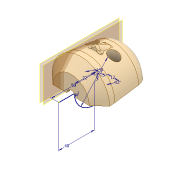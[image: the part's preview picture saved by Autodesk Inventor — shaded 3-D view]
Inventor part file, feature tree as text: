
AUTODESK INVENTOR PART (.ipt)
format: ipt  version: 2017 (Build 210142000, 142)  size: 439,808 bytes
history: native  units: mm
features: sketch x14, extrude x11, fillet x7, chamfer x2, plane x2, projected_geometry x2, revolve x1, thicken_offset x1
ambient origin geometry x8: Origin, YZ Plane, XZ Plane, XY Plane, X Axis, Y Axis, Z Axis, Center Point
bodies: Solid1 (feature_tree)
feature tree (40):
  revolve  "Revolution1"  [1 undecoded]
  fillet  "Fillet1"  Radius=30.0mm
  chamfer  "Chamfer1"  Distance=10.0mm Angle=45.0deg
  fillet  "Fillet2"  Radius=20.0mm
  fillet  "Fillet3"  Radius=60.0mm
  thicken_offset  "Thicken1"
  extrude  "Extrusion1"  Depth=4.0mm
  sketch  "Sketch3"  dims[d4=20.0mm d5=10.0mm d6=20.0mm d7=45.0deg d8=20.0mm d9=60.0mm]
  extrude  "Extrusion2"  Depth=50.0mm
  extrude  "Extrusion3"  Depth=12.0mm
  fillet  "Fillet4"  Radius=12.0mm
  fillet  "Fillet5"  Radius=12.0mm
  extrude  "Extrusion4"  Depth=10.0mm TaperAngle=0.0deg
  fillet  "Fillet6"  Radius=6.0mm
  fillet  "Fillet7"  Radius=2.0mm
  extrude  "Extrusion5"  Depth=5.0mm
  sketch  "Sketch7"  dims[d20=10.0mm d21=0.0mm d22=10.0mm d23=0.0mm d24=6.0mm d25=2.0mm]
  plane  "Work Plane1"
  extrude  "Extrusion6"  Depth=2.0mm
  extrude  "Extrusion7"  Depth=40.0mm
  extrude  "Extrusion8"  Depth=45.0mm
  plane  "Work Plane2"
  extrude  "Extrusion9"  Depth=40.0mm TaperAngle=0.0deg
  sketch  "Sketch12"  dims[d35=40.0mm d36=40.0mm d37=0.0mm]
  extrude  "Extrusion10"  Depth=4.0mm
  extrude  "Extrusion11"  [1 undecoded]
  chamfer  "Chamfer2"  Distance=20.5mm
  sketch  "Sketch1"  dims[d0=40.0mm d1=80.0mm d2=30.0mm]
  sketch  "Sketch2"  dims[d3=90.0deg]
  sketch  "Sketch4"  dims[d10=4.0mm d11=4.0mm]
  sketch  "Sketch5"  dims[d12=0.0mm d13=0.0mm d14=50.0mm]
  sketch  "Sketch6"  dims[d15=12.0mm d16=12.0mm d17=12.0mm d18=12.0mm]
  sketch  "Sketch8"  dims[d26=5.0mm d27=5.0mm]
  sketch  "Sketch9"  dims[d28=32.0mm d29=0.0mm d30=2.0mm]
  projected_geometry  "Projected Loop1"
  sketch  "Sketch10"  dims[d31=56.0mm d32=40.0mm]
  projected_geometry  "Projected Loop2"
  sketch  "Sketch11"  dims[d33=1.5mm d34=45.0mm]
  sketch  "Sketch13"  dims[d38=22.0mm d39=4.0mm]
  sketch  "Sketch14"  dims[d40=6.0mm d41=-8.0mm d42=20.5mm d43=0.0mm d44=25.0mm d45=6.0mm d46=0.0mm d47=12.0mm d48=0.0mm d49=-3.75mm d50=2.0mm d51=0.0mm d52=28.0mm d53=2.0mm d54=0.0mm d55=10.0mm d56=0.0mm d57=0.0mm d58=11.0mm d59=2.0mm d60=45.0deg]
note: 2 required parameter values undecoded (feature->parameter linkage not recoverable at this tier; creation-order binding heuristic only, values carry confidence <= 0.55)